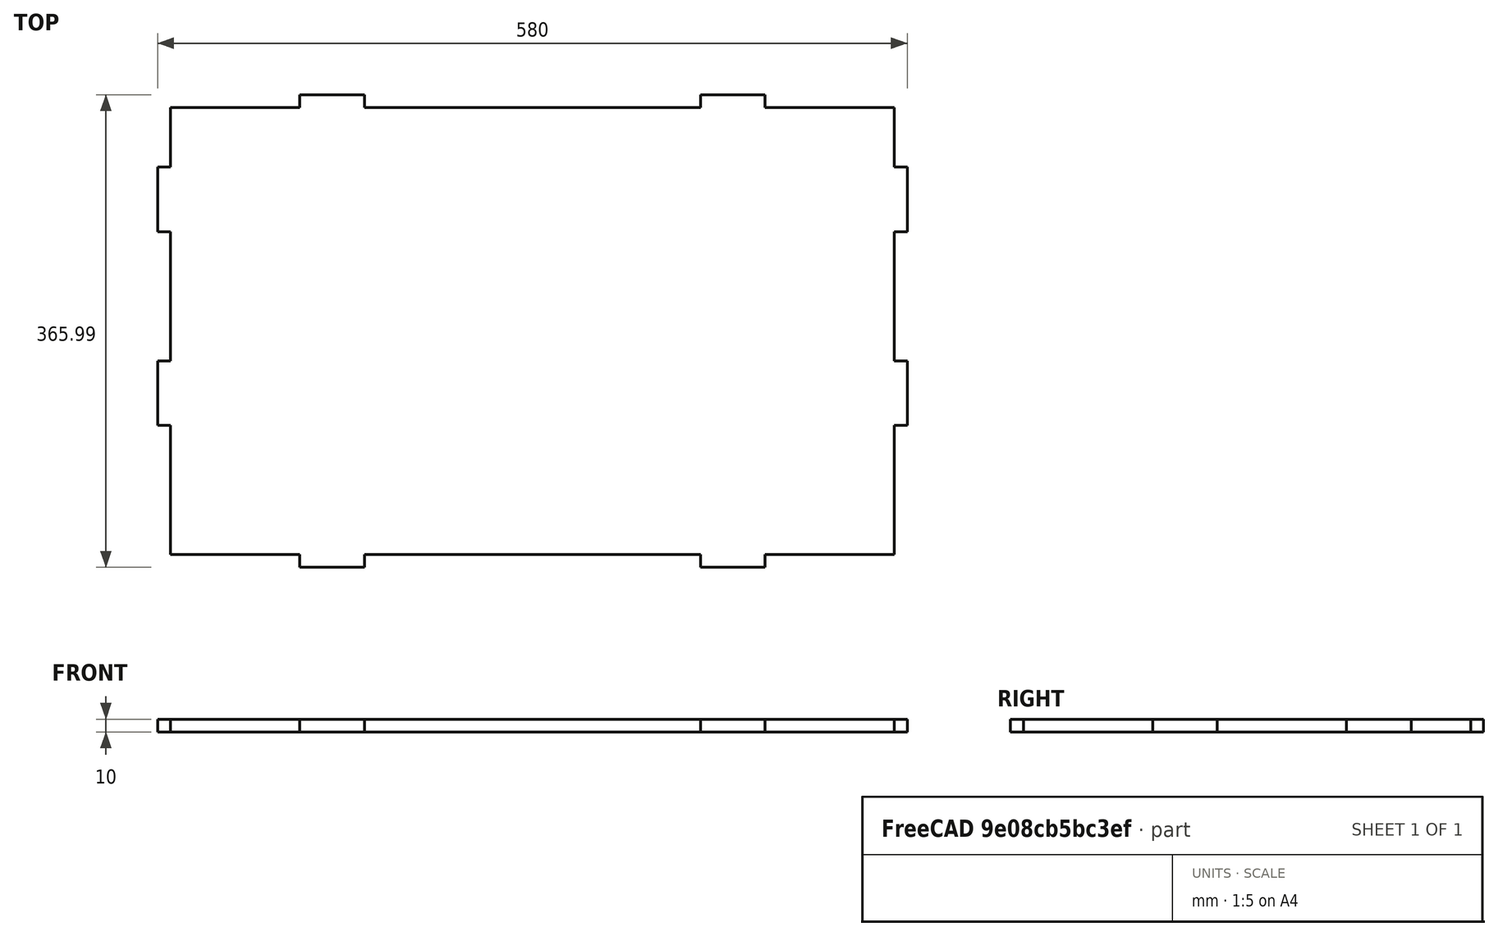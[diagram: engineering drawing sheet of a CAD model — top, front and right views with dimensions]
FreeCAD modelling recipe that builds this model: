
FCSTD DOCUMENT  (FreeCAD 0.16R)
Label: bottom
License: All rights reserved
LicenseURL: http://fr.wikipedia.org/wiki/<copyright redacted>
objects: Sketcher::SketchObject×1, PartDesign::Pad×1
note: 3 computed .brp shape members not serialized (recipe doc carries the construction recipe); baked Part::Feature solids carry a one-line shape summary decoded from their .brp

FEATURE [Sketcher::SketchObject] Sketch
  sketch-geometry (36):
    g0: LineSegment StartX=560 StartY=300 StartZ=0 EndX=570 EndY=300 EndZ=0
    g1: LineSegment StartX=570 StartY=300 StartZ=0 EndX=570 EndY=250 EndZ=0
    g2: LineSegment StartX=570 StartY=250 StartZ=0 EndX=560 EndY=250 EndZ=0
    g3: LineSegment StartX=560 StartY=150 StartZ=0 EndX=570 EndY=150 EndZ=0
    g4: LineSegment StartX=570 StartY=150 StartZ=0 EndX=570 EndY=100 EndZ=0
    g5: LineSegment StartX=570 StartY=100 StartZ=0 EndX=560 EndY=100 EndZ=0
    g6: LineSegment StartX=560 StartY=345.986 StartZ=0 EndX=560 EndY=300 EndZ=0
    g7: LineSegment StartX=560 StartY=250 StartZ=0 EndX=560 EndY=150 EndZ=0
    g8: LineSegment StartX=560 StartY=100 StartZ=0 EndX=560 EndY=0 EndZ=0
    g9: LineSegment StartX=-10 StartY=300 StartZ=0 EndX=0 EndY=300 EndZ=0
    g10: LineSegment StartX=0 StartY=250 StartZ=0 EndX=-10 EndY=250 EndZ=0
    g11: LineSegment StartX=-10 StartY=250 StartZ=0 EndX=-10 EndY=300 EndZ=0
    g12: LineSegment StartX=-10 StartY=150 StartZ=0 EndX=0 EndY=150 EndZ=0
    g13: LineSegment StartX=0 StartY=100 StartZ=0 EndX=-10 EndY=100 EndZ=0
    g14: LineSegment StartX=-10 StartY=100 StartZ=0 EndX=-10 EndY=150 EndZ=0
    g15: LineSegment StartX=100 StartY=355.986 StartZ=0 EndX=150 EndY=355.986 EndZ=0
    g16: LineSegment StartX=150 StartY=355.986 StartZ=0 EndX=150 EndY=345.986 EndZ=0
    g17: LineSegment StartX=100 StartY=345.986 StartZ=0 EndX=100 EndY=355.986 EndZ=0
    g18: LineSegment StartX=460 StartY=355.986 StartZ=0 EndX=410 EndY=355.986 EndZ=0
    g19: LineSegment StartX=410 StartY=355.986 StartZ=0 EndX=410 EndY=345.986 EndZ=0
    g20: LineSegment StartX=460 StartY=345.986 StartZ=0 EndX=460 EndY=355.986 EndZ=0
    g21: LineSegment StartX=100 StartY=-10 StartZ=0 EndX=150 EndY=-10 EndZ=0
    g22: LineSegment StartX=150 StartY=-10 StartZ=0 EndX=150 EndY=0 EndZ=0
    g23: LineSegment StartX=100 StartY=0 StartZ=0 EndX=100 EndY=-10 EndZ=0
    g24: LineSegment StartX=410 StartY=-10 StartZ=0 EndX=460 EndY=-10 EndZ=0
    g25: LineSegment StartX=460 StartY=-10 StartZ=0 EndX=460 EndY=0 EndZ=0
    g26: LineSegment StartX=410 StartY=0 StartZ=0 EndX=410 EndY=-10 EndZ=0
    g27: LineSegment StartX=560 StartY=345.986 StartZ=0 EndX=460 EndY=345.986 EndZ=0
    g28: LineSegment StartX=150 StartY=345.986 StartZ=0 EndX=410 EndY=345.986 EndZ=0
    g29: LineSegment StartX=100 StartY=345.986 StartZ=0 EndX=0 EndY=345.986 EndZ=0
    g30: LineSegment StartX=0 StartY=345.986 StartZ=0 EndX=0 EndY=300 EndZ=0
    g31: LineSegment StartX=0 StartY=250 StartZ=0 EndX=0 EndY=150 EndZ=0
    g32: LineSegment StartX=0 StartY=100 StartZ=0 EndX=0 EndY=0 EndZ=0
    g33: LineSegment StartX=100 StartY=0 StartZ=0 EndX=0 EndY=0 EndZ=0
    g34: LineSegment StartX=150 StartY=0 StartZ=0 EndX=410 EndY=0 EndZ=0
    g35: LineSegment StartX=460 StartY=0 StartZ=0 EndX=560 EndY=0 EndZ=0
  constraints (108):
    c: Coincident(g0,g1)
    c: Coincident(g1,g2)
    c: Horizontal(g0)
    c: Horizontal(g2)
    c: Vertical(g1)
    c: Coincident(g3,g4)
    c: Coincident(g4,g5)
    c: Horizontal(g3)
    c: Horizontal(g5)
    c: Vertical(g4)
    c: Coincident(g6,g0)
    c: Coincident(g7,g2)
    c: Coincident(g7,g3)
    c: Vertical(g7)
    c: Coincident(g8,g5)
    c: Vertical(g8)
    c: Vertical(g6)
    c: DistanceY(g8,g6) = 345.986
    c: Coincident(g10,g11)
    c: Coincident(g11,g9)
    c: Horizontal(g9)
    c: Horizontal(g10)
    c: Vertical(g11)
    c: Coincident(g13,g14)
    c: Coincident(g14,g12)
    c: Horizontal(g12)
    c: Horizontal(g13)
    c: Vertical(g14)
    c: Coincident(g15,g16)
    c: Coincident(g17,g15)
    c: Horizontal(g15)
    c: Vertical(g16)
    c: Vertical(g17)
    c: Coincident(g18,g19)
    c: Coincident(g20,g18)
    c: Horizontal(g18)
    c: Vertical(g19)
    c: Vertical(g20)
    c: Coincident(g21,g22)
    c: Coincident(g23,g21)
    c: Horizontal(g21)
    c: Vertical(g22)
    c: Vertical(g23)
    c: Coincident(g24,g25)
    c: Coincident(g26,g24)
    c: Horizontal(g24)
    c: Vertical(g25)
    c: Vertical(g26)
    c: DistanceX(g-1,g8) = 560
    c: Equal(g0,g20)
    c: Equal(g20,g19)
    c: Equal(g19,g2)
    c: Equal(g2,g3)
    c: Equal(g3,g5)
    c: Equal(g5,g25)
    c: Equal(g25,g26)
    c: Equal(g26,g22)
    c: Equal(g22,g23)
    c: Equal(g23,g13)
    c: Equal(g13,g12)
    c: Equal(g12,g10)
    c: Equal(g10,g9)
    c: Equal(g9,g17)
    c: Equal(g17,g16)
    c: Equal(g18,g15)
    c: Equal(g15,g1)
    c: Equal(g1,g4)
    c: Equal(g4,g24)
    c: Equal(g24,g21)
    c: Equal(g21,g14)
    c: Equal(g14,g11)
    c: Distance(g0) = 10
    c: Distance(g1) = 50
    c: Coincident(g27,g6)
    c: Coincident(g27,g20)
    c: Horizontal(g27)
    c: Coincident(g28,g16)
    c: Coincident(g28,g19)
    c: Horizontal(g28)
    c: Coincident(g29,g17)
    c: PointOnObject(g29,g-2)
    c: Horizontal(g29)
    c: Coincident(g30,g29)
    c: Coincident(g30,g9)
    c: Vertical(g30)
    c: Coincident(g31,g10)
    c: Coincident(g31,g12)
    c: Vertical(g31)
    c: Coincident(g32,g13)
    c: Coincident(g32,g-1)
    c: Coincident(g33,g23)
    c: Coincident(g33,g-1)
    c: Horizontal(g33)
    c: Coincident(g34,g22)
    c: Coincident(g34,g26)
    c: Horizontal(g34)
    c: Coincident(g35,g25)
    c: Coincident(g35,g8)
    c: Horizontal(g35)
    c: Equal(g33,g29)
    c: Equal(g29,g27)
    c: Equal(g27,g35)
    c: Distance(g29) = 100
    c: Equal(g7,g31)
    c: Equal(g30,g6)
    c: Equal(g32,g8)
    c: Distance(g2,g3) = 100
    c: DistanceY(g8,g5) = 100
FEATURE [PartDesign::Pad] Pad
  Length = 10
  Length2 = 100
  Sketch = -> Sketch
  Type = 0
